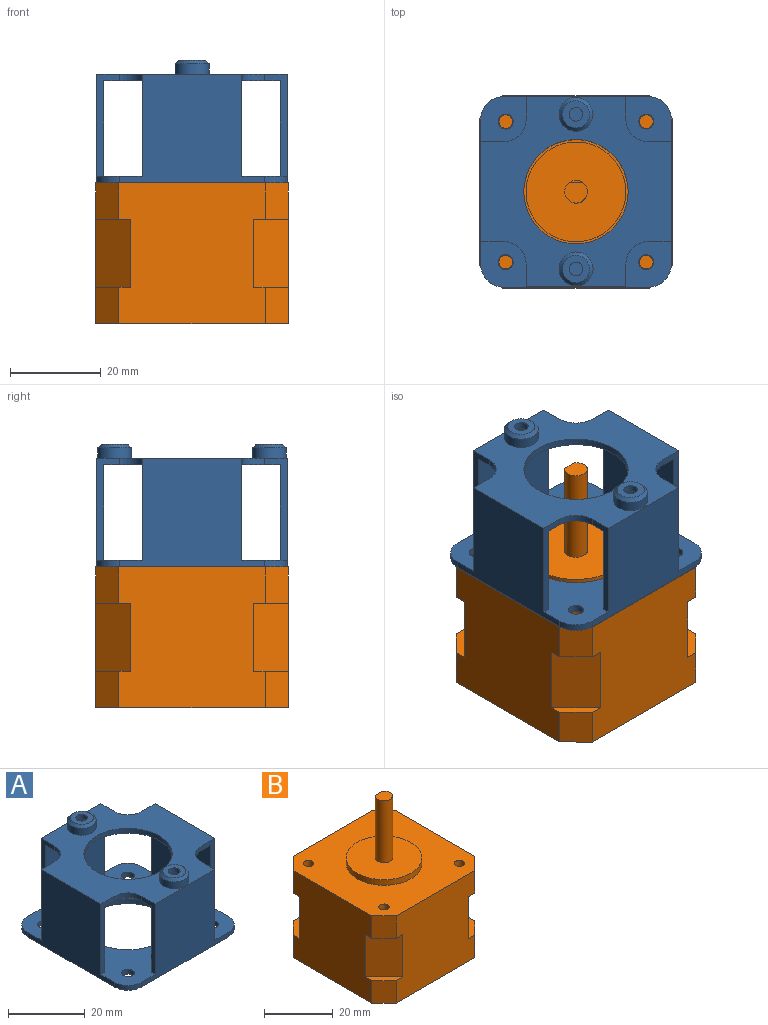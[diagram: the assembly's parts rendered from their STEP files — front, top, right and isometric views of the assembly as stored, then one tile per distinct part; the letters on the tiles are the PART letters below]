
ASSEMBLY  parts=2 mates=1
PART A: 46 faces, bbox 42x42x27 mm
  f0: cylinder r=2.25mm len=4.5mm, axis (0,0,1), area 42.4mm2, adj f30,f42
  f1: cylinder r=2.25mm len=4.5mm, axis (0,0,1), area 42.4mm2, adj f30,f40
  f2: plane 22x21mm, normal (0,1,0), area 462mm2, adj f6,f26,f27,f30
  f3: plane 22x21mm, normal (0,-1,0), area 462mm2, adj f6,f21,f22,f30
  f4: plane 22x21mm, normal (-1,0,0), area 462mm2, adj f6,f24,f25,f30
  f5: plane 22x21mm, normal (1,0,0), area 462mm2, adj f6,f28,f29,f30
  f6: plane 42x42mm, normal (0,0,1), area 1160.9mm2, adj f2,f3,f4,f5,f7,f8,f9,f10
  f7: plane 32x24mm, normal (-1,0,0), area 543mm2, adj f6,f8,f19,f20,f23,f28,f29
  f8: cylinder r=5mm len=5mm, axis (0,0,-1), area 11.8mm2, adj f6,f7,f9,f20
  f9: plane 32x24mm, normal (0,-1,0), area 543mm2, adj f6,f8,f10,f20,f23,f26,f27
  f10: cylinder r=5mm len=5mm, axis (0,0,-1), area 11.8mm2, adj f6,f9,f11,f20
  f11: plane 32x24mm, normal (1,0,0), area 543mm2, adj f6,f10,f12,f20,f23,f24,f25
  f12: cylinder r=5mm len=5mm, axis (0,0,-1), area 11.8mm2, adj f6,f11,f13,f20
  f13: plane 32x24mm, normal (0,1,0), area 543mm2, adj f6,f12,f19,f20,f21,f22,f23
  f14: cylinder r=11.5mm len=23mm, axis (0,0,-1), area 108.4mm2, adj f6,f20
  f15: cylinder r=1.65mm len=3.3mm, axis (0,0,-1), area 15.6mm2, adj f6,f20
  f16: cylinder r=1.65mm len=3.3mm, axis (0,0,-1), area 15.6mm2, adj f6,f20
  f17: cylinder r=1.65mm len=3.3mm, axis (0,0,-1), area 15.6mm2, adj f6,f20
  f18: cylinder r=1.65mm len=3.3mm, axis (0,0,-1), area 15.6mm2, adj f6,f20
  f19: cylinder r=5mm len=5mm, axis (0,0,-1), area 11.8mm2, adj f6,f7,f13,f20
  f20: plane 42x42mm, normal (0,0,-1), area 1292.9mm2, adj f7,f8,f9,f10,f11,f12,f13,f14
  f21: plane 22.5x5mm, normal (-1,0,0), area 39mm2, adj f3,f6,f13,f23,f30,f33
  f22: plane 22.5x5mm, normal (1,0,0), area 39mm2, adj f3,f6,f13,f23,f30,f32
  f23: plane 42x42mm, normal (0,0,1), area 881.6mm2, adj f7,f9,f11,f13,f21,f22,f24,f25
  f24: plane 22.5x5mm, normal (0,1,0), area 39mm2, adj f4,f6,f11,f23,f30,f32
  f25: plane 22.5x5mm, normal (0,-1,0), area 39mm2, adj f4,f6,f11,f23,f30,f31
  f26: plane 22.5x5mm, normal (1,0,0), area 39mm2, adj f2,f6,f9,f23,f30,f31
  f27: plane 22.5x5mm, normal (-1,0,0), area 39mm2, adj f2,f6,f9,f23,f30,f34
  f28: plane 22.5x5mm, normal (0,1,0), area 39mm2, adj f5,f6,f7,f23,f30,f33
  f29: plane 22.5x5mm, normal (0,-1,0), area 39mm2, adj f5,f6,f7,f23,f30,f34
  f30: plane 39x39mm, normal (0,0,-1), area 806.2mm2, adj f0,f1,f2,f3,f4,f5,f21,f22
  f31: cylinder r=5mm len=5mm, axis (0,0,1), area 11.8mm2, adj f23,f25,f26,f30
  f32: cylinder r=5mm len=5mm, axis (0,0,1), area 11.8mm2, adj f22,f23,f24,f30
  f33: cylinder r=5mm len=5mm, axis (0,0,1), area 11.8mm2, adj f21,f23,f28,f30
  f34: cylinder r=5mm len=5mm, axis (0,0,1), area 11.8mm2, adj f23,f27,f29,f30
  f35: cylinder r=11.5mm len=23mm, axis (0,0,1), area 108.4mm2, adj f23,f30
  f36: cylinder r=3.75mm len=7.5mm, axis (0,0,-1), area 53mm2, adj f23,f44
  f37: plane 6x6mm, normal (0,0,1), area 21.2mm2, adj f41,f44
  f38: cylinder r=3.75mm len=7.5mm, axis (0,0,-1), area 53mm2, adj f23,f45
  f39: plane 6x6mm, normal (0,0,1), area 21.2mm2, adj f43,f45
  f40: plane 4.5x4.5mm, normal (0,0,-1), area 8.8mm2, adj f1,f41
  f41: cylinder r=1.5mm len=3mm, axis (0,0,1), area 14.1mm2, adj f37,f40
  f42: plane 4.5x4.5mm, normal (0,0,-1), area 8.8mm2, adj f0,f43
  f43: cylinder r=1.5mm len=3mm, axis (0,0,1), area 14.1mm2, adj f39,f42
  f44: cone r=3mm half-angle=45deg, axis (0,0,-1), area 22.5mm2, adj f36,f37
  f45: cone r=3mm half-angle=45deg, axis (0,0,-1), area 22.5mm2, adj f38,f39
PART B: 48 faces, bbox 42.4x42.4x55 mm
  f0: plane 32.26x31mm, normal (0,1,0), area 923.8mm2, adj f6,f7,f9,f10,f12,f15,f16,f19
  f1: plane 32.26x31mm, normal (-1,0,0), area 923.8mm2, adj f5,f6,f10,f11,f12,f14,f15,f18
  f2: plane 32.26x31mm, normal (0,-1,0), area 923.8mm2, adj f4,f5,f8,f11,f12,f13,f14,f17
  f3: plane 32.26x31mm, normal (1,0,0), area 923.8mm2, adj f4,f7,f8,f9,f12,f13,f16,f17
  f4: plane 15x7.62mm, normal (0.71,-0.71,0), area 161.6mm2, adj f2,f3,f8,f17
  f5: plane 15x7.62mm, normal (-0.71,-0.71,0), area 161.6mm2, adj f1,f2,f11,f18
  f6: plane 15x7.62mm, normal (-0.71,0.71,0), area 161.6mm2, adj f0,f1,f10,f19
  f7: plane 15x7.62mm, normal (0.71,0.71,0), area 161.6mm2, adj f0,f3,f9,f20
  f8: plane 7.62x7.62mm, normal (0,0,-1), area 16.1mm2, adj f2,f3,f4,f13
  f9: plane 7.62x7.62mm, normal (0,0,-1), area 16.1mm2, adj f0,f3,f7,f16
  f10: plane 7.62x7.62mm, normal (0,0,-1), area 16.1mm2, adj f0,f1,f6,f15
  f11: plane 7.62x7.62mm, normal (0,0,-1), area 16.1mm2, adj f1,f2,f5,f14
  f12: plane 42.42x42.42mm, normal (0,0,1), area 1339.4mm2, adj f0,f1,f2,f3,f13,f14,f15,f16
  f13: plane 8x5.08mm, normal (0.71,-0.71,0), area 57.5mm2, adj f2,f3,f8,f12
  f14: plane 8x5.08mm, normal (-0.71,-0.71,0), area 57.5mm2, adj f1,f2,f11,f12
  f15: plane 8x5.08mm, normal (-0.71,0.71,0), area 57.5mm2, adj f0,f1,f10,f12
  f16: plane 8x5.08mm, normal (0.71,0.71,0), area 57.5mm2, adj f0,f3,f9,f12
  f17: plane 7.62x7.62mm, normal (0,0,1), area 16.1mm2, adj f2,f3,f4,f24
  f18: plane 7.62x7.62mm, normal (0,0,1), area 16.1mm2, adj f1,f2,f5,f21
  f19: plane 7.62x7.62mm, normal (0,0,1), area 16.1mm2, adj f0,f1,f6,f22
  f20: plane 7.62x7.62mm, normal (0,0,1), area 16.1mm2, adj f0,f3,f7,f23
  f21: plane 8x5.08mm, normal (-0.71,-0.71,0), area 57.5mm2, adj f1,f2,f18,f25
  f22: plane 8x5.08mm, normal (-0.71,0.71,0), area 57.5mm2, adj f0,f1,f19,f25
  f23: plane 8x5.08mm, normal (0.71,0.71,0), area 57.5mm2, adj f0,f3,f20,f25
  f24: plane 8x5.08mm, normal (0.71,-0.71,0), area 57.5mm2, adj f2,f3,f17,f25
  f25: plane 42.42x42.42mm, normal (0,0,-1), area 1719.4mm2, adj f0,f1,f2,f3,f21,f22,f23,f24
  f26: cylinder r=11mm len=22mm, axis (0,0,-1), area 138.2mm2, adj f12,f27
  f27: plane 22x22mm, normal (0,0,1), area 360.4mm2, adj f26,f28
  f28: cylinder r=2.5mm len=22mm, axis (0,0,-1), area 297.3mm2, adj f27,f29,f30,f31
  f29: plane 5x4.5mm, normal (0,0,1), area 18.6mm2, adj f28,f31
  f30: plane 3x0.5mm, normal (0,0,1), area 1mm2, adj f28,f31
  f31: plane 15x3mm, normal (0,1,0), area 45mm2, adj f28,f29,f30
  f32: cylinder r=1.5mm len=6.35mm, axis (0,0,1), area 59.8mm2, adj f12,f33
  f33: plane 3x3mm, normal (0,0,1), area 7.1mm2, adj f32
  f34: cylinder r=1.5mm len=6.35mm, axis (0,0,1), area 59.8mm2, adj f12,f35
  f35: plane 3x3mm, normal (0,0,1), area 7.1mm2, adj f34
  f36: cylinder r=1.5mm len=6.35mm, axis (0,0,1), area 59.8mm2, adj f12,f37
  f37: plane 3x3mm, normal (0,0,1), area 7.1mm2, adj f36
  f38: cylinder r=1.5mm len=6.35mm, axis (0,0,1), area 59.8mm2, adj f12,f39
  f39: plane 3x3mm, normal (0,0,1), area 7.1mm2, adj f38
  f40: cylinder r=1.5mm len=6.35mm, axis (0,0,-1), area 59.8mm2, adj f25,f41
  f41: plane 3x3mm, normal (0,0,-1), area 7.1mm2, adj f40
  f42: cylinder r=1.5mm len=6.35mm, axis (0,0,-1), area 59.8mm2, adj f25,f43
  f43: plane 3x3mm, normal (0,0,-1), area 7.1mm2, adj f42
  f44: cylinder r=1.5mm len=6.35mm, axis (0,0,-1), area 59.8mm2, adj f25,f45
  f45: plane 3x3mm, normal (0,0,-1), area 7.1mm2, adj f44
  f46: cylinder r=1.5mm len=6.35mm, axis (0,0,-1), area 59.8mm2, adj f25,f47
  f47: plane 3x3mm, normal (0,0,-1), area 7.1mm2, adj f46
PLACE A t=(21.21,16.13,22.5)mm
PLACE B t=(42.21,-4.87,7)mm
MATE fastened A.f14 <-> B.f26  axis (0,0,-1) through (42.21,-4.87,22.5)mm
